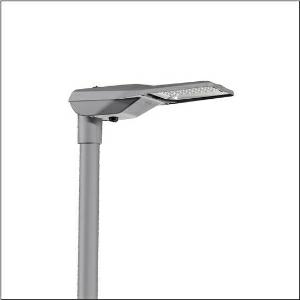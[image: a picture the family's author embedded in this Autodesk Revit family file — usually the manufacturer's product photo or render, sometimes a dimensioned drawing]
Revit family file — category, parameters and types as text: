
# Revit family: streetlight_sl_21_mini___st0_5a_5xe2b43t08hb_0266
name_source: partatom
category: Lighting Fixtures
units: mm (PartAtom-declared; Revit-internal decimal feet)

## family parameters
Cut with Voids When Loaded = No
Host = Face
Light Source = No
Part Type = Normal
Room Calculation Point = No
Round Connector Dimension = Use Diameter
Shared = No

## types (1)
- --- (1 x LED, 9430 lm, 66 W, 4000K)
    Apparent Load = 66 VA
    CIE Flux Codes = 41 75 97 100 100
    Color Rendering = 70
    Color Temperature = 4000K
    Default Elevation = 1800 mm
    Description = Streetlight SL 21 mini, mast luminaire, primary light control with lens, of PMMA, primary optical cover: cover, of toughened safety glass, transparent, light distribution: ST0.5a, light emission: direct distribution, primary light characteristic: asymmetric, installation type: side-entry, post-top, LED, High Power LED, rated luminous flux: 9.430lm, luminous efficacy: 143lm/W, light colour: 740, colour temperature: 4000K, control gear: D4i, control: overheat protection, constant luminous flux control, time-dependent luminous flux control, flexible luminous flux parameterisation, pre-setting: logarithmic dimming characteristic, mains connection: 220..240V, AC, 50/60Hz, start of lifetime: 66W, end of service life: 69W, reduction: 30W, luminaire housing, of diecast aluminium, powder-coated, SITECO metallic grey (DB 702S), corrosivity category C5 high according to DIN EN ISO 12944, please order mast flange separately, inclination adjustable: 0°, 5°, 10°, 15°, sealing non-destructively replaceable, multi-level sealing system, length: 628mm, width: 235mm, height: 110mm, mast flange for spigot size: 42mm (side-entry): 5XC10008XM4, 60/48mm (side-entry/post-top): 5XC10108XM2, 76/60mm (side-entry/post-top): 5XC10108XM1, mounting height: 4..8m, Smart Interface below and above, protection rating (complete): IP66, insulation class (complete): insulation class II (safety insulation), certification: CE, ENEC, ENEC+, VDE, impact resistance: IK10, permissible operating ambient temperature for outdoor applications: -40..+50°C, standard-compliant lighting for roads and squares, packaging unit: 1 piece

Light Distribution: ST0.5a
    Height = 110 mm
    Lamp = 1 x LED
    Lamp Light Flux = 9430 lm
    Lamp Power = 66 W
    Lamp count = 1
    Length = 625 mm
    Luminous efficacy = 143 lm/W
    Manufacturer = Siteco
    ModVariant = No
    Model = 5XE2B43T08HB
    Number of Poles = 1
    OnlyDefault = Yes
    Power Factor = 1
    Product Name = Streetlight SL 21 mini | ST0.5a
    Product group = mast luminaire | pylon top
    ProductGroupID = 6100
    Protection Class = Protection class II
    Protection Degree = IP 66
    RLX_Detail_Level = 1
    RLX_Emergency_Light_Flux = 0 lm
    RLX_Emergency_Type = 0
    RLX_Emergency_Type_DB = No
    RlxData = <blob elided: 37349 chars, md5=45555779>
    Socket = socket
    Standby Power = 0 W
    System Light Flux = 9430 lm
    System Power = 66 W
    Type Comments = factory setting: luminous flux: 100 % | dim-lin: 254 | 670 mA
    Type Image = l_1003514.jpg
    URL = http://relux.com
    VarID = @adj_188467
    Voltage = 0 V
    Weight = 0.00 kg
    Width = 234 mm

## geometry (parser evidence)
native form markers: Blend x4, Sweep x11
no freeform markers — native parametric forms only
